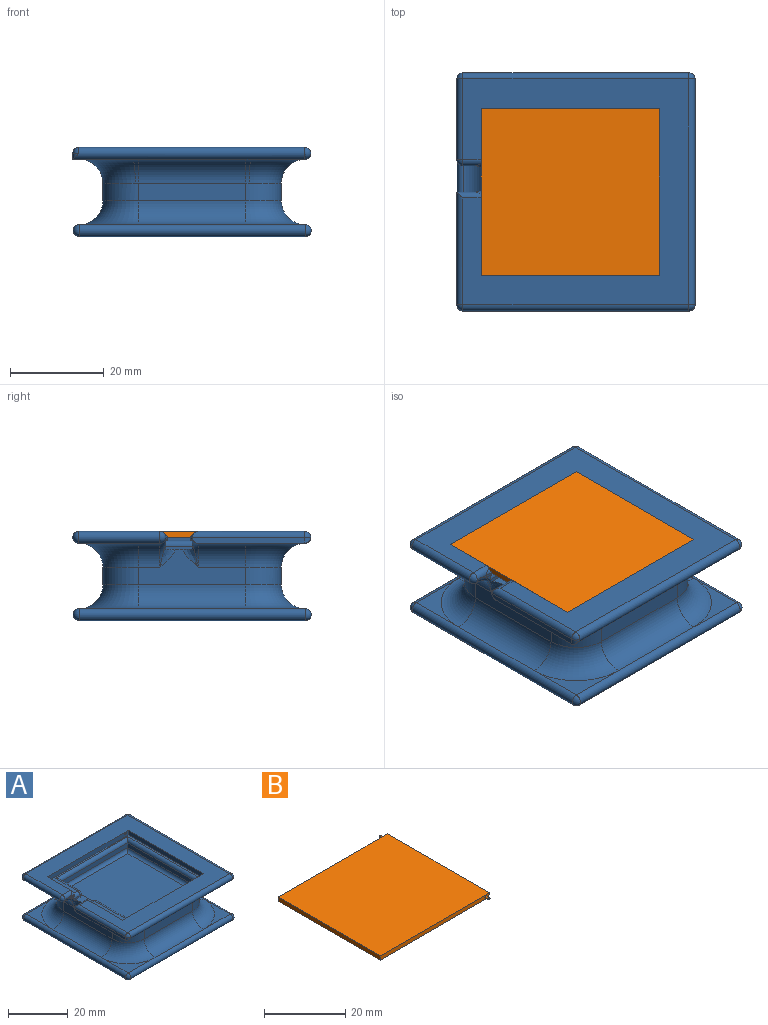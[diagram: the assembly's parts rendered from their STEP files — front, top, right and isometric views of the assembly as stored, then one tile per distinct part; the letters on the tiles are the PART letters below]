
ASSEMBLY  parts=2 mates=1
PART A: 117 faces, bbox 59x59x20.2 mm
  f0: plane 3.15x0.65mm, normal (0,-1,0), area 1.8mm2, adj f3,f100,f110,f112
  f1: plane 3.13x0.65mm, normal (0,1,0), area 1.8mm2, adj f4,f100,f106,f108
  f2: plane 22.86x7.62mm, normal (-1,0,0), area 103.2mm2, adj f3,f4,f43,f44,f47,f55,f57,f100
  f3: bspline ~6.89x3.81mm, area 7.4mm2, adj f0,f2,f76,f80,f83,f100,f101,f103
  f4: bspline ~6.09x3.81mm, area 7.4mm2, adj f1,f2,f78,f82,f87,f100,f102,f104
  f5: plane 38.1x35.56mm, normal (0,0,1), area 156.5mm2, adj f7,f83,f84,f85,f86,f87,f92,f93
  f6: plane 31.75x1.91mm, normal (1,0,0), area 55.3mm2, adj f7,f90,f91,f93,f97,f100,f108,f112
  f7: cylinder r=1.27mm len=10.26mm, axis (0,1,0), area 19.2mm2, adj f5,f6,f92,f111
  f8: plane 48.25x48.25mm, normal (0,0,1), area 941.8mm2, adj f23,f25,f26,f28,f29,f31,f32,f83
  f9: plane 11.37x11.07mm, normal (0,0,-1), area 32.8mm2, adj f28,f32,f64
  f10: plane 48.25x17.3mm, normal (0,0,-1), area 72.3mm2, adj f23,f25,f26,f28,f57,f59,f61,f63
  f11: plane 12.7x12.7mm, normal (0,0,1), area 34.6mm2, adj f36,f40,f52
  f12: plane 12.7x12.7mm, normal (0,0,1), area 34.6mm2, adj f36,f37,f53
  f13: plane 12.7x12.7mm, normal (0,0,1), area 34.6mm2, adj f40,f41,f48
  f14: plane 3.81x2.77mm, normal (0,1,0), area 4.8mm2, adj f43,f50,f61,f68
  f15: plane 22.86x3.81mm, normal (0,-1,0), area 87.1mm2, adj f44,f45,f51,f60
  f16: plane 22.86x3.81mm, normal (1,0,0), area 87.1mm2, adj f45,f46,f54,f67
  f17: plane 12.7x12.7mm, normal (0,0,1), area 34.6mm2, adj f37,f41,f49
  f18: plane 48.26x48.26mm, normal (0,0,-1), area 2329mm2, adj f36,f37,f40,f41
  f19: plane 2.54x0.53mm, normal (0,1,0), area 0.4mm2, adj f29,f78,f82
  f20: plane 24.07x1.27mm, normal (-1,0,0), area 30.2mm2, adj f22,f29,f31,f34
  f21: plane 2.54x0.53mm, normal (0,-1,0), area 0.4mm2, adj f26,f76,f80
  f22: plane 22.8x12.83mm, normal (0,0,-1), area 64.9mm2, adj f20,f29,f32,f55,f56
  f23: cylinder r=1.27mm len=17.3mm, axis (0,1,0), area 69mm2, adj f8,f10,f24,f77
  f24: sphere r=1.27mm, area 5.1mm2, adj f23,f25
  f25: cylinder r=1.27mm len=48.25mm, axis (-1,0,0), area 192.5mm2, adj f8,f10,f24,f27
  f26: cylinder r=1.27mm len=3.9mm, axis (1,0,0), area 7.1mm2, adj f8,f10,f21,f76,f77,f79,f83
  f27: sphere r=1.27mm, area 5.1mm2, adj f25,f28
  f28: cylinder r=1.27mm len=48.25mm, axis (0,1,0), area 192.1mm2, adj f8,f9,f10,f27,f30,f65,f66,f67
  f29: cylinder r=1.27mm len=5.17mm, axis (-1,0,0), area 11.1mm2, adj f8,f19,f20,f22,f31,f78,f81,f87
  f30: sphere r=1.27mm, area 5.1mm2, adj f28,f32
  f31: cylinder r=1.27mm len=24.07mm, axis (0,-1,0), area 46.8mm2, adj f8,f20,f29,f33
  f32: cylinder r=1.27mm len=49.52mm, axis (1,0,0), area 193.5mm2, adj f8,f9,f22,f30,f33,f34,f58,f60
  f33: sphere r=1.27mm, area 2.5mm2, adj f31,f32,f34
  f34: cylinder r=1.27mm len=1.27mm, axis (0,0,1), area 1.3mm2, adj f20,f32,f33
  f35: sphere r=1.27mm, area 5.1mm2, adj f36,f37
  f36: cylinder r=1.27mm len=48.26mm, axis (0,-1,0), area 192.5mm2, adj f11,f12,f18,f35,f38,f54
  f37: cylinder r=1.27mm len=48.26mm, axis (-1,0,0), area 192.5mm2, adj f12,f17,f18,f35,f39,f51
  f38: sphere r=1.27mm, area 5.1mm2, adj f36,f40
  f39: sphere r=1.27mm, area 5.1mm2, adj f37,f41
  f40: cylinder r=1.27mm len=48.26mm, axis (1,0,0), area 192.5mm2, adj f11,f13,f18,f38,f42,f50
  f41: cylinder r=1.27mm len=48.26mm, axis (0,1,0), area 192.5mm2, adj f13,f17,f18,f39,f42,f47
  f42: sphere r=1.27mm, area 5.1mm2, adj f40,f41
  f43: cylinder r=7.62mm len=7.62mm, axis (0,0,1), area 45.6mm2, adj f2,f14,f48,f59
  f44: cylinder r=7.62mm len=7.62mm, axis (0,0,-1), area 45.6mm2, adj f2,f15,f49,f56,f58
  f45: cylinder r=7.62mm len=7.62mm, axis (0,0,1), area 45.6mm2, adj f15,f16,f53,f62,f64,f66
  f46: cylinder r=7.62mm len=8.89mm, axis (0,0,-1), area 47.2mm2, adj f16,f52,f63,f65,f70,f71,f72,f74
  f47: cylinder r=5.08mm len=22.86mm, axis (0,-1,0), area 182.4mm2, adj f2,f41,f48,f49
  f48: torus R=12.7mm, axis (0,0,1), area 118.7mm2, adj f13,f43,f47,f50
  f49: torus R=12.7mm, axis (0,0,1), area 118.7mm2, adj f17,f44,f47,f51
  f50: cylinder r=5.08mm len=22.86mm, axis (-1,0,0), area 182.4mm2, adj f14,f40,f48,f52,f72
  f51: cylinder r=5.08mm len=22.86mm, axis (1,0,0), area 182.4mm2, adj f15,f37,f49,f53
  f52: torus R=12.7mm, axis (0,0,1), area 118.7mm2, adj f11,f46,f50,f54
  f53: torus R=12.7mm, axis (0,0,1), area 118.7mm2, adj f12,f45,f51,f54
  f54: cylinder r=5.08mm len=22.86mm, axis (0,1,0), area 182.4mm2, adj f16,f36,f52,f53
  f55: cylinder r=5.08mm len=10.16mm, axis (0,1,0), area 81.1mm2, adj f2,f22,f56,f78
  f56: torus R=12.7mm, axis (0,0,1), area 111.3mm2, adj f22,f44,f55,f58
  f57: cylinder r=5.08mm len=5.08mm, axis (0,1,0), area 36.3mm2, adj f2,f10,f59,f76
  f58: bspline ~5.22x5.18mm, area 7.3mm2, adj f32,f44,f56,f60
  f59: torus R=12.7mm, axis (0,0,1), area 118.7mm2, adj f10,f43,f57,f61
  f60: cylinder r=5.08mm len=22.86mm, axis (1,0,0), area 181.3mm2, adj f15,f32,f58,f62
  f61: cylinder r=5.08mm len=22.86mm, axis (1,0,0), area 182.4mm2, adj f10,f14,f59,f63,f70
  f62: bspline ~5.22x5.18mm, area 7.3mm2, adj f32,f45,f60,f64
  f63: torus R=12.7mm, axis (0,0,1), area 109.3mm2, adj f10,f46,f61,f65
  f64: torus R=12.7mm, axis (0,0,1), area 102mm2, adj f9,f45,f62,f66
  f65: bspline ~7.12x5.58mm, area 9.3mm2, adj f28,f46,f63,f67
  f66: bspline ~7.12x5.58mm, area 9.3mm2, adj f28,f45,f64,f67
  f67: cylinder r=5.08mm len=22.86mm, axis (0,1,0), area 180.6mm2, adj f16,f28,f65,f66
  f68: cylinder r=1.91mm len=19.05mm, axis (0,1,0), area 197.6mm2, adj f14,f69,f70,f72,f73
  f69: plane 3.81x3.81mm, normal (0,1,0), area 11.4mm2, adj f68
  f70: plane 20.09x5.08mm, normal (0,0,-1), area 95.7mm2, adj f46,f61,f68,f73,f74
  f71: plane 5.08x1.27mm, normal (-1,0,0), area 6.5mm2, adj f46,f73,f74,f75
  f72: plane 20.09x5.08mm, normal (0,0,1), area 95.7mm2, adj f46,f50,f68,f73,f75
  f73: plane 20.09x3.81mm, normal (0,1,0), area 70.2mm2, adj f68,f70,f71,f72,f74,f75
  f74: cylinder r=1.27mm len=5.08mm, axis (0,-1,0), area 10mm2, adj f46,f70,f71,f73
  f75: cylinder r=1.27mm len=5.08mm, axis (0,-1,0), area 10mm2, adj f46,f71,f72,f73
  f76: torus R=6.35mm, axis (0,-1,0), area 9.1mm2, adj f3,f21,f26,f57
  f77: sphere r=1.27mm, area 5.1mm2, adj f23,f26
  f78: torus R=6.35mm, axis (0,-1,0), area 9.1mm2, adj f4,f19,f29,f55
  f79: bspline ~3.04x3.04mm, area 0.6mm2, adj f26,f80,f83
  f80: cylinder r=2.54mm len=1.27mm, axis (0,0,1), area 0.7mm2, adj f3,f21,f79,f83
  f81: bspline ~3.04x3.04mm, area 0.6mm2, adj f29,f82,f87
  f82: cylinder r=2.54mm len=1.27mm, axis (0,0,-1), area 0.7mm2, adj f4,f19,f81,f87
  f83: plane 13.39x4mm, normal (1,0,0), area 23.6mm2, adj f3,f5,f8,f26,f79,f80,f86,f101
  f84: plane 38.1x1.91mm, normal (0,1,0), area 72.3mm2, adj f5,f8,f85,f87,f115
  f85: plane 35.56x1.91mm, normal (-1,0,0), area 67.7mm2, adj f5,f8,f84,f86
  f86: plane 38.1x1.91mm, normal (0,-1,0), area 72.3mm2, adj f5,f8,f83,f85,f113
  f87: plane 19x3.98mm, normal (1,0,0), area 34.2mm2, adj f4,f5,f8,f29,f81,f82,f84,f102
  f88: plane 29.21x29.11mm, normal (0,0,1), area 850.4mm2, adj f96,f97,f98,f99
  f89: plane 31.75x1.91mm, normal (-1,0,0), area 60.5mm2, adj f90,f91,f94,f98
  f90: plane 31.65x1.91mm, normal (0,1,0), area 60.3mm2, adj f6,f89,f95,f99
  f91: plane 31.65x1.91mm, normal (0,-1,0), area 60.3mm2, adj f6,f89,f92,f96
  f92: cylinder r=1.27mm len=34.19mm, axis (1,0,0), area 65.7mm2, adj f5,f7,f91,f94
  f93: cylinder r=1.27mm len=15.89mm, axis (0,1,0), area 30.4mm2, adj f5,f6,f95,f107
  f94: cylinder r=1.27mm len=34.29mm, axis (0,-1,0), area 65.9mm2, adj f5,f89,f92,f95
  f95: cylinder r=1.27mm len=34.19mm, axis (-1,0,0), area 65.7mm2, adj f5,f90,f93,f94
  f96: cylinder r=1.27mm len=31.65mm, axis (-1,0,0), area 60.6mm2, adj f88,f91,f97,f98
  f97: cylinder r=1.27mm len=31.75mm, axis (0,-1,0), area 60.8mm2, adj f6,f88,f96,f99
  f98: cylinder r=1.27mm len=31.75mm, axis (0,1,0), area 60.8mm2, adj f88,f89,f96,f99
  f99: cylinder r=1.27mm len=31.65mm, axis (1,0,0), area 60.6mm2, adj f88,f90,f97,f98
  f100: plane 8.14x3.97mm, normal (0,0,1), area 19.5mm2, adj f0,f1,f2,f3,f4,f6,f108,f112
  f101: plane 1.21x1.15mm, normal (0,-1,0), area 0.7mm2, adj f3,f83,f103
  f102: plane 1.19x1mm, normal (0,1,0), area 0.6mm2, adj f4,f87,f104
  f103: plane 1.2x0.38mm, normal (0,0,-1), area 0.1mm2, adj f3,f83,f101
  f104: plane 1.04x0.36mm, normal (0,0,-1), area 0.1mm2, adj f4,f87,f102
  f105: bspline ~1.27x1.27mm, area 0.1mm2, adj f4,f5,f87,f106
  f106: cylinder r=1.27mm len=3.11mm, axis (-1,0,0), area 6.2mm2, adj f1,f5,f105,f107
  f107: sphere r=1.27mm, area 3.5mm2, adj f93,f106,f108
  f108: cylinder r=1.27mm len=1.27mm, axis (0,0,1), area 1.3mm2, adj f1,f6,f100,f107
  f109: bspline ~1.31x1.31mm, area 0.1mm2, adj f3,f5,f83,f110
  f110: cylinder r=1.27mm len=3.13mm, axis (1,0,0), area 6.2mm2, adj f0,f5,f109,f111
  f111: sphere r=1.27mm, area 3.5mm2, adj f7,f110,f112
  f112: cylinder r=1.27mm len=1.27mm, axis (0,0,-1), area 1.3mm2, adj f0,f6,f100,f111
  f113: cylinder r=0.32mm len=2.54mm, axis (0,-1,0), area 5.1mm2, adj f86,f114
  f114: plane 0.64x0.64mm, normal (0,-1,0), area 0.3mm2, adj f113
  f115: cylinder r=0.32mm len=2.54mm, axis (0,1,0), area 5.1mm2, adj f84,f116
  f116: plane 0.64x0.64mm, normal (0,1,0), area 0.3mm2, adj f115
PART B: 12 faces, bbox 38.1x38.1x1.3 mm
  f0: plane 38.1x1.27mm, normal (0,1,0), area 47.7mm2, adj f1,f3,f4,f5,f9
  f1: plane 35.56x1.27mm, normal (-1,0,0), area 45.2mm2, adj f0,f2,f3,f4
  f2: plane 38.1x1.27mm, normal (0,-1,0), area 47.7mm2, adj f1,f3,f4,f5,f6
  f3: plane 38.1x35.56mm, normal (0,0,1), area 1354.8mm2, adj f0,f1,f2,f5
  f4: plane 36.83x35.56mm, normal (0,0,-1), area 1309.7mm2, adj f0,f1,f2,f5
  f5: cylinder r=1.27mm len=35.56mm, axis (0,1,0), area 70.9mm2, adj f0,f2,f3,f4
  f6: cylinder r=0.32mm len=1.02mm, axis (0,1,0), area 2mm2, adj f2,f8
  f7: plane 0.13x0.13mm, normal (0,-1,0), area 0mm2, adj f8
  f8: torus R=0.06mm, axis (0,-1,0), area 0.6mm2, adj f6,f7
  f9: cylinder r=0.32mm len=1.02mm, axis (0,-1,0), area 2mm2, adj f0,f11
  f10: plane 0.13x0.13mm, normal (0,1,0), area 0mm2, adj f11
  f11: torus R=0.06mm, axis (0,1,0), area 0.6mm2, adj f9,f10
PLACE A t=(-5.1,5.88,-3.87)mm
PLACE B t=(-7.04,-1.58,13.91)mm
MATE revolute B.f6 <-> A.f113  axis (0,1,0) through (10.53,18.04,14.55)mm
